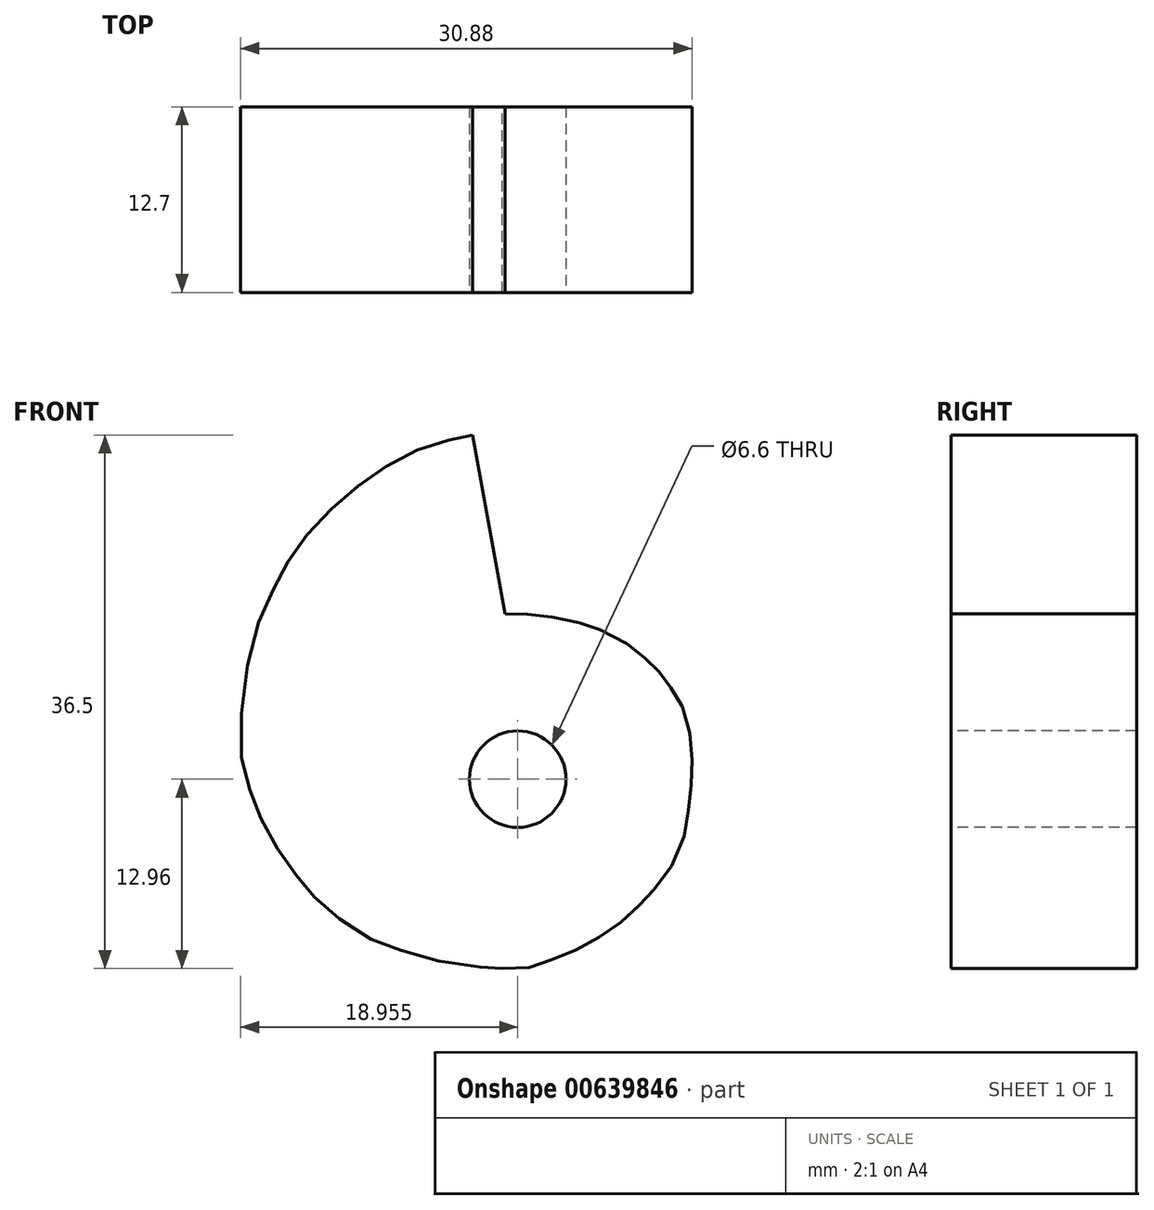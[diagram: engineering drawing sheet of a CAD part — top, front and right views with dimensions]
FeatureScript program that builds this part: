
annotation { "Feature Type Name" : "Feature", "Feature Type Description" : "" }
export const myFeature = defineFeature(function(context is Context, id is Id, definition is map)
    precondition{}
    {
        {
            var Q0;
            Q0=qCreatedBy(makeId("Front.planeOp"),FACE);
            var sketch = newSketch(context, id + "F0", { "sketchPlane" : qUnion([Q0])});
            skFitSpline(sketch, "E0", {"points": [v(-1.66, 11.3) * mm, v(-0.38, 11.3) * mm, v(1.01, 11.18) * mm, v(2.99, 10.83) * mm, v(4.23, 10.44) * mm, v(5.74, 9.82) * mm, v(7.68, 8.5) * mm, v(7.99, 8.2) * mm, v(8.8, 7.42) * mm, v(9.46, 6.57) * mm, v(10, 5.83) * mm, v(10.7, 4.32) * mm, v(11.05, 2.46) * mm, v(11.13, 0.67) * mm, v(11.01, -0.88) * mm, v(10.82, -2.54) * mm, v(10.45, -4.4) * mm, v(9.19, -6.8) * mm, v(8.1, -8.02) * mm, v(7.32, -8.84) * mm, v(5.95, -10.04) * mm, v(4.53, -10.97) * mm, v(2.97, -11.8) * mm, v(1.42, -12.42) * mm, v(0, -12.88) * mm, v(-1.86, -12.94) * mm], "startDerivative": vector(35.47, 0.56) * mm, "endDerivative": vector(-44.43, 1.41) * mm});
            skFitSpline(sketch, "E1", {"points": [v(-1.86, -12.94) * mm, v(-2.2, -12.94) * mm, v(-5.1, -12.65) * mm, v(-8.8, -11.7) * mm, v(-11.06, -10.82) * mm, v(-13.83, -8.9) * mm, v(-15.23, -7.43) * mm, v(-16.57, -5.74) * mm, v(-18.03, -3.42) * mm, v(-18.94, -1.2) * mm, v(-19.63, 1.07) * mm, v(-19.57, 5.76) * mm, v(-18.53, 10.67) * mm, v(-17.3, 13.37) * mm, v(-16.23, 15.35) * mm, v(-14.48, 17.51) * mm, v(-12.31, 19.57) * mm, v(-10.12, 21.18) * mm, v(-7.49, 22.58) * mm, v(-5.21, 23.27) * mm, v(-3.87, 23.54) * mm], "startDerivative": vector(-13.9, -0.4) * mm, "endDerivative": vector(34.85, 6.63) * mm});
            skLineSegment(sketch, "E2", {"start": v(-3.87, 23.54) * mm, "end": v(-1.66, 11.3) * mm});
            skSolve(sketch);
        }
        {
            var Q0;
            Q0=makeQuery(id+"F0.imprint","IMPRINT",FACE,{"disambiguationData":[TD([[makeQuery(id+"F0.imprint","IMPRINT",EDGE,{"derivedFrom":sQuery(id+"F0.wireOp",EDGE,"E0")}),-1.0]])]});
            extrude(context, id + "F1", {"entities" : qUnion([Q0]), "depth" : 12.7 * mm, "offsetDistance" : 25.4 * mm});
        }
        {
            var Q0;
            Q0=makeQuery(id+"F1.opExtrude","CAP_FACE",FACE,{"disambiguationData":[OSD([sQuery(id+"F0.wireOp",EDGE,"E0"),sQuery(id+"F0.wireOp",EDGE,"E1"),sQuery(id+"F0.wireOp",EDGE,"E2")])],"isStart":false});
            var sketch = newSketch(context, id + "F2", { "sketchPlane" : qUnion([Q0])});
            skCircle(sketch, "E3", {"center": v(-0.8, 0) * mm, "radius": 3.3 * mm});
            skSolve(sketch);
        }
        {
            var Q0;
            Q0=makeQuery(id+"F2.imprint","IMPRINT",FACE,{"disambiguationData":[TD([[makeQuery(id+"F2.imprint","IMPRINT",EDGE,{"derivedFrom":sQuery(id+"F2.wireOp",EDGE,"E3")}),1.0]])]});
            extrude(context, id + "F3", {"entities" : qUnion([Q0]), "operationType" : NewBodyOperationType.REMOVE, "oppositeDirection" : true, "depth" : 12.7 * mm, "offsetDistance" : 25.4 * mm});
        }
    });
